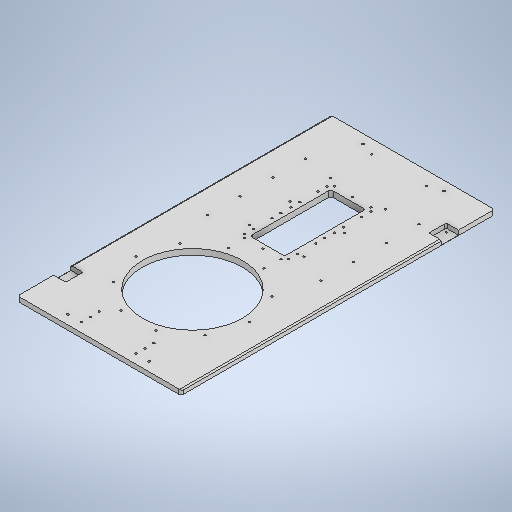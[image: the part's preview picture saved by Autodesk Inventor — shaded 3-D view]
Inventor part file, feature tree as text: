
AUTODESK INVENTOR PART (.ipt)
format: ipt  version: 2025 (Build 290162000, 162)  size: 640,512 bytes
history: native  units: in
note: dims shown in document units (in); Inventor stores cm internally (conversion verified against a paired STEP export)
features: sketch x17, extrude x6, hole x5, fillet x3, chamfer x3, plane x2
ambient origin geometry x8: Origin, YZ Plane, XZ Plane, XY Plane, X Axis, Y Axis, Z Axis, Center Point
bodies: Solid1 (feature_tree)
feature tree (36):
  extrude  "Base Cover"  Depth=14.1732in
  sketch  "Sketch2"  dims[d5=8.6614in d6=0.0in d7=0.0in]
  extrude  "Cylinder Hole"  Depth=0.503in
  plane  "Work Plane1"
  hole  "Hole3"  [1 undecoded]
  sketch  "Sketch7"  dims[d69=0.1575in d70=3.937in d72=360.0deg]
  plane  "Work Plane2"
  hole  "Hole4"  [1 undecoded]
  sketch  "Sketch9"  dims[d82=1.063in]
  fillet  "Rounded Side Corners"  Radius=7.0625in
  chamfer  "Chamfer1"  Distance=3.937in Angle=360.0deg
  chamfer  "Chamfer2"  Distance=0.1969in
  extrude  "Magnet Seats"  Depth=0.3937in TaperAngle=45.0deg
  hole  "Hole5"  [1 undecoded]
  chamfer  "Chamfer5"  Distance=0.1181in
  hole  "Hole6"  [1 undecoded]
  sketch  "Sketch15"  dims[d85=1.4961in]
  extrude  "Extrusion11"  Depth=0.3937in TaperAngle=0.0deg
  fillet  "Fillet3"  Radius=0.748in
  hole  "Hole7"  [1 undecoded]
  fillet  "Rounded Bottom Corners"  Radius=0.8661in
  extrude  "Extrusion14"  Depth=0.3937in
  extrude  "Extrusion15"  Depth=0.3937in
  sketch  "Sketch1"  dims[d0=14.1732in d1=27.1654in]
  sketch  "Sketch6"  dims[d68=9.8425in]
  sketch  "Sketch8"  dims[d74=0.1628in d75=0.3937in d76=0.1575in d77=0.0787in d78=90.0deg d79=0.3937in d80=0.8108in]
  sketch  "Sketch Circular Pattern4"  dims[d57=0.1936in d58=0.1969in d59=0.1575in d60=0.0787in d61=90.0deg d62=0.1969in d63=0.8108in]
  sketch  "Sketch11"  dims[d83=1.063in]
  sketch  "Sketch12"  dims[d84=1.4961in]
  sketch  "Sketch Rectangular Pattern1"  dims[d2=0.503in d3=0.0in d4=8.0709in]
  sketch  "Sketch Rectangular Pattern2"  dims[d8=10.6299in d50=5.9055in d55=7.0625in]
  sketch  "Sketch Rectangular Pattern3"  dims[d56=25.5906in]
  sketch  "Sketch Rectangular Pattern4"  dims[d64=10.3543in]
  sketch  "Sketch Rectangular Pattern5"  dims[d65=10.6299in]
  sketch  "Sketch18"  dims[d86=3.1102in]
  sketch  "Sketch19"  dims[d87=3.1102in d88=0.1969in d89=0.0984in d90=0.0787in d91=45.0deg d92=0.0984in d93=0.0787in d94=45.0deg d95=0.1181in d96=0.1181in d97=0.3848in d98=0.0in d109=0.748in d110=0.315in d111=0.8661in d112=0.748in d113=0.1299in d114=0.1299in d115=0.1299in d116=0.1299in d118=0.315in d119=0.8661in d120=0.748in d121=0.748in d122=0.1276in d123=0.315in d124=0.1575in d125=0.0787in d126=90.0deg d127=0.315in d128=0.8108in d129=0.0138in d130=0.0787in d131=45.0deg d146=3.9469in d147=0.7874in d148=0.3937in d149=0.1575in d150=3.937in d152=1.1811in d153=0.3937in d155=0.3937in d157=0.1575in d158=1.1811in d160=0.7874in d161=0.3937in d163=0.3937in d165=9.8425in d166=0.1575in d167=2.9528in d168=1.1811in d169=3.1496in d171=1.4173in d172=0.3937in d174=0.3937in d176=0.1628in d177=0.3937in d178=0.1575in d179=0.0787in d180=90.0deg d181=0.3937in d182=0.8108in d191=3.0in d192=7.0in d193=6.4961in d194=0.8312in d195=0.0in d196=0.1969in d197=0.3937in d198=0.1969in d199=1.9685in d201=0.7874in d202=0.3937in d204=0.3937in d206=0.3189in d207=0.1969in d208=0.3189in d209=1.9685in d211=0.7874in d212=0.3937in d214=0.3937in d216=0.1628in d217=0.3937in d218=0.1575in d219=0.0787in d220=90.0deg d221=0.3937in d222=0.8108in d230=0.2756in d243=0.1378in d244=0.0787in d245=0.3848in d246=0.0in d247=0.1378in d248=0.0787in d249=0.3937in d250=0.0in d26=0.0394in d27=0.0394in d28=0.0394in d29=0.0059in d30=0.0098in d31=0.0148in d32=0.5635in d33=0.0295in d34=0.8108in d35=0.0025in d36=0.0295in d37=0.0148in d66=0.0197in d67=0.0344in]
note: 5 required parameter values undecoded (feature->parameter linkage not recoverable at this tier; creation-order binding heuristic only, values carry confidence <= 0.55)
